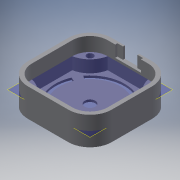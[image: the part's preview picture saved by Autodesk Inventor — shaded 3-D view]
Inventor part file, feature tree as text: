
AUTODESK INVENTOR PART (.ipt)
format: ipt  version: 2018 (Build 220112000, 112)  size: 378,368 bytes
history: native  units: mm
features: reference x21, extrude x10, sketch x9, projected_geometry x8, other x4, plane x1, pattern_circular x1
ambient origin geometry x8: Origin, YZ Plane, XZ Plane, XY Plane, X Axis, Y Axis, Z Axis, Center Point
bodies: Volumenkörper1 (feature_tree)
feature tree (54):
  other  "Querschnitt1"
  other  "Querschnitt2"
  extrude  "Extrusion1"  Depth=10.0mm
  plane  "Arbeitsebene1"
  extrude  "Extrusion2"  Depth=6.0mm
  extrude  "Extrusion3"  Depth=8.5mm TaperAngle=0.0deg
  extrude  "Extrusion4"  Depth=4.5mm
  extrude  "Extrusion5"  Depth=4.5mm
  extrude  "Extrusion6"  Depth=1.5mm TaperAngle=0.0deg
  extrude  "Extrusion7"  Depth=8.0mm TaperAngle=0.0deg
  extrude  "Extrusion8"  Depth=45.0mm
  pattern_circular  "Runde Anordnung1"  [2 undecoded]
  extrude  "Extrusion9"  Depth=1.5mm TaperAngle=0.0deg
  extrude  "Extrusion10"  Depth=1.5mm
  sketch  "Skizze1"  dims[d0=10.0mm d1=0.0mm d2=6.0mm]
  reference  "Referenz1"
  sketch  "Skizze2"  dims[d3=6.0mm d4=6.0mm]
  projected_geometry  "Projizierte Kontur1"
  reference  "Referenz2"
  reference  "Referenz3"
  sketch  "Skizze3"  dims[d5=6.0mm d6=8.5mm d7=0.0mm]
  reference  "Referenz4"
  reference  "Referenz5"
  reference  "Referenz6"
  reference  "Referenz7"
  reference  "Referenz8"
  reference  "Referenz9"
  reference  "Referenz10"
  sketch  "Skizze4"  dims[d8=4.5mm d9=4.5mm]
  projected_geometry  "Projizierte Kontur2"
  reference  "Referenz11"
  reference  "Referenz12"
  projected_geometry  "Projizierte Kontur3"
  sketch  "Skizze6"  dims[d10=4.5mm d11=4.5mm]
  reference  "Referenz13"
  sketch  "Skizze7"  dims[d12=0.15mm d13=1.5mm d14=0.0mm]
  sketch  "Skizze8"  dims[d15=1.5mm d16=0.0mm d19=8.0mm d20=0.0mm]
  reference  "Referenz14"
  reference  "Referenz15"
  reference  "Referenz16"
  reference  "Referenz17"
  reference  "Referenz18"
  reference  "Referenz19"
  reference  "Referenz20"
  reference  "Referenz21"
  projected_geometry  "Projizierte Kontur4"
  projected_geometry  "Projizierte Kontur5"
  projected_geometry  "Projizierte Kontur6"
  sketch  "Skizze9"  dims[d21=5.0mm d22=0.0mm d23=45.0mm]
  projected_geometry  "Projizierte Kontur7"
  sketch  "Skizze10"  dims[d24=1.5mm d25=1.5mm d26=5.75mm d27=0.0mm d29=3.0mm d30=3.0mm d31=2.0mm d32=0.0mm d33=30.0mm d34=360.0deg d36=10.0mm d39=0.5mm d40=2.0mm d41=-5.25mm d42=20.0mm d43=0.5mm d44=2.0mm d45=-28.25mm d46=20.0mm d47=1.5mm d48=0.0mm d49=1.5mm d50=0.0mm]
  projected_geometry  "Projizierte Kontur8"
  parser-record x1  (decoder bookkeeping rows leaked as tree rows — omitted from the tree; the rows remain in map.json)
  other  "VolumeKnob.iam"
note: 2 required parameter values undecoded (feature->parameter linkage not recoverable at this tier; creation-order binding heuristic only, values carry confidence <= 0.55)
note: 1 file-system path scrubbed to <path> (originals preserved in map.json)
